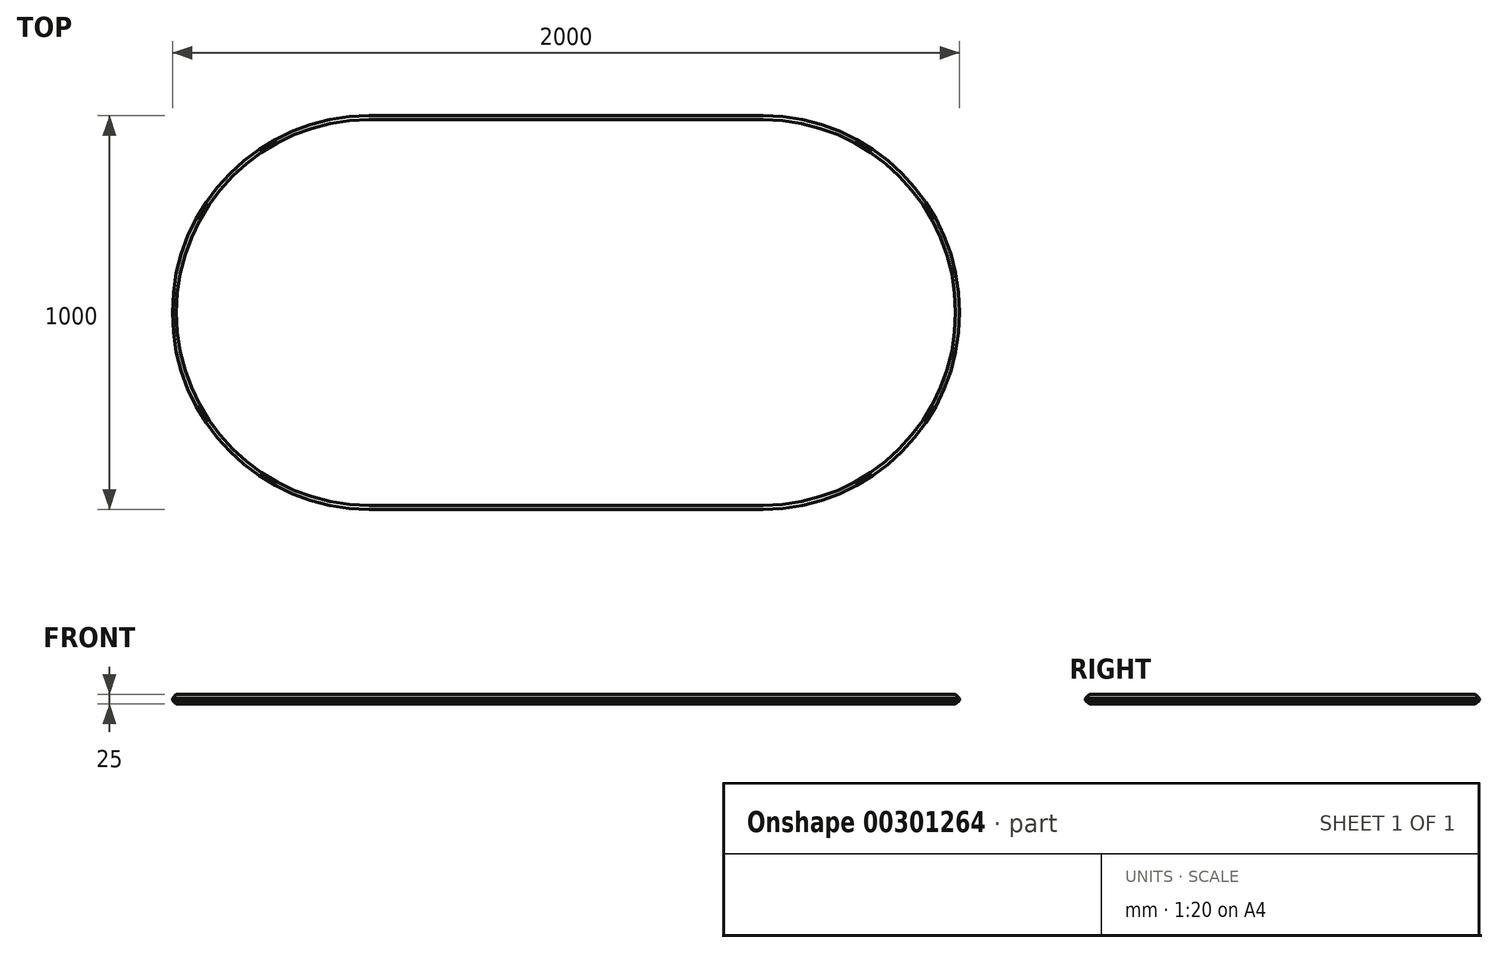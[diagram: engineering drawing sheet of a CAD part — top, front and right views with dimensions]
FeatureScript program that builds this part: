
annotation { "Feature Type Name" : "Feature", "Feature Type Description" : "" }
export const myFeature = defineFeature(function(context is Context, id is Id, definition is map)
    precondition{}
    {
        {
            var Q0;
            Q0=qCreatedBy(makeId("Top.planeOp"),FACE);
            var sketch = newSketch(context, id + "F0", { "sketchPlane" : qUnion([Q0])});
            skArc(sketch, "E0", {"start": v(0, -56.88) * mm, "mid": v(500, 443.12) * mm, "end": v(0, 943.12) * mm});
            skLineSegment(sketch, "E1", {"start": v(0, 943.12) * mm, "end": v(0, -56.88) * mm});
            skLineSegment(sketch, "E2.bottom", {"start": v(0, 943.12) * mm, "end": v(0, 943.12) * mm});
            skLineSegment(sketch, "E2.top", {"start": v(0, -56.88) * mm, "end": v(0, -56.88) * mm});
            skLineSegment(sketch, "E3.bottom", {"start": v(-1000, -56.88) * mm, "end": v(0, -56.88) * mm});
            skLineSegment(sketch, "E3.top", {"start": v(-1000, 943.12) * mm, "end": v(0, 943.12) * mm});
            skLineSegment(sketch, "E3.left", {"start": v(-1000, -56.88) * mm, "end": v(-1000, 943.12) * mm});
            skArc(sketch, "E4", {"start": v(-1000, 943.12) * mm, "mid": v(-1500, 443.12) * mm, "end": v(-1000, -56.88) * mm});
            skSolve(sketch);
        }
        {
            var Q0;
            Q0 = qSketchRegion(id + "F0", true);
            extrude(context, id + "F1", {"entities" : qUnion([Q0]), "oppositeDirection" : true, "depth" : 25 * mm});
        }
        {
            var Q0;
            Q0=makeQuery(id+"F1.opExtrude","CAP_FACE",FACE,{"disambiguationData":[OSD([sQuery(id+"F0.wireOp",EDGE,"E0"),sQuery(id+"F0.wireOp",EDGE,"E3.bottom"),sQuery(id+"F0.wireOp",EDGE,"E3.top"),sQuery(id+"F0.wireOp",EDGE,"E4")])],"isStart":false});
            chamfer(context, id + "F2", {"entities" : qUnion([Q0]), "width" : 10 * mm, "tangentPropagation" : true});
        }
        {
            var Q0;
            Q0=makeQuery(id+"F1.opExtrude","CAP_EDGE",EDGE,{"disambiguationData":[OSD([sQuery(id+"F0.wireOp",EDGE,"E3.top")])],"isStart":true});
            chamfer(context, id + "F3", {"entities" : qUnion([Q0]), "width" : 10 * mm, "tangentPropagation" : true});
        }
    });
